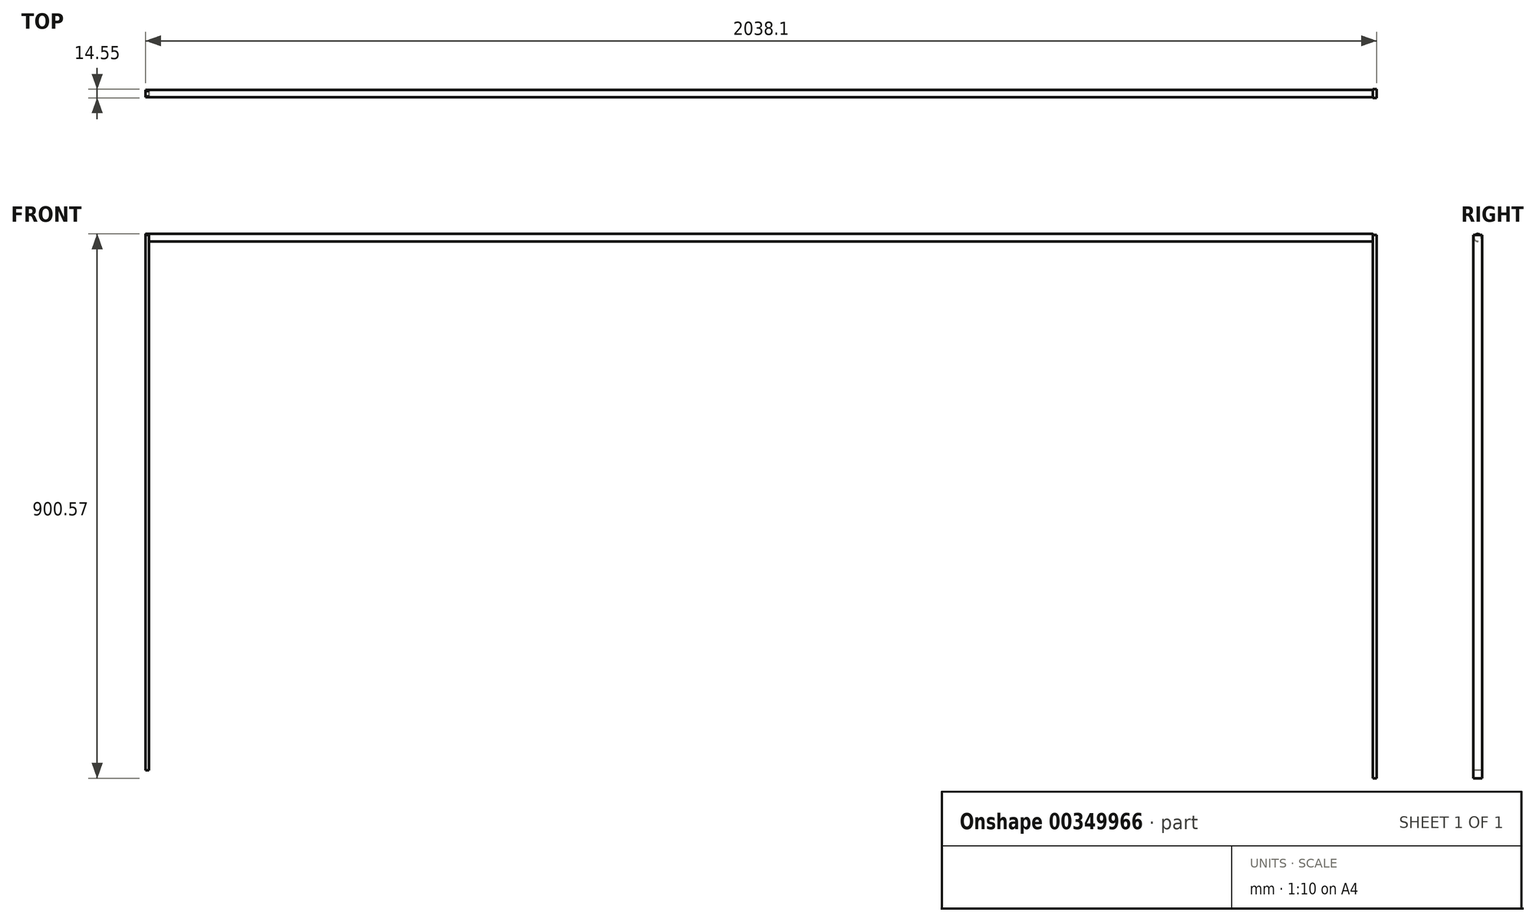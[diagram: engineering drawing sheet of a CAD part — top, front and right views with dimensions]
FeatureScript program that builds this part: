
annotation { "Feature Type Name" : "Feature", "Feature Type Description" : "" }
export const myFeature = defineFeature(function(context is Context, id is Id, definition is map)
    precondition{}
    {
        {
            var Q0;
            Q0=qCreatedBy(makeId("Right.planeOp"),FACE);
            var sketch = newSketch(context, id + "F0", { "sketchPlane" : qUnion([Q0])});
            skCircle(sketch, "E0", {"center": v(-52.21, 53.51) * mm, "radius": 6.09 * mm});
            skSolve(sketch);
        }
        {
            var Q0;
            Q0 = qSketchRegion(id + "F0", true);
            extrude(context, id + "F1", {"entities" : qUnion([Q0]), "depth" : 2032 * mm, "offsetDistance" : 25.4 * mm});
        }
        {
            var Q0;
            Q0=qCreatedBy(makeId("Right.planeOp"),FACE);
            var sketch = newSketch(context, id + "F2", { "sketchPlane" : qUnion([Q0])});
            skLineSegment(sketch, "E1.bottom", {"start": v(-45.98, 57.67) * mm, "end": v(-58.45, 57.67) * mm});
            skLineSegment(sketch, "E1.top", {"start": v(-45.98, -65.98) * mm, "end": v(-58.45, -65.98) * mm});
            skLineSegment(sketch, "E1.left", {"start": v(-45.98, 57.67) * mm, "end": v(-45.98, -65.98) * mm});
            skLineSegment(sketch, "E1.right", {"start": v(-58.45, 57.67) * mm, "end": v(-58.45, -65.98) * mm});
            skSolve(sketch);
        }
        {
            var Q0;
            Q0 = qSketchRegion(id + "F2", true);
            extrude(context, id + "F3", {"entities" : qUnion([Q0]), "operationType" : NewBodyOperationType.ADD, "depth" : 5.33 * mm});
        }
        {
            var Q0;
            Q0=makeQuery(id+"F1.opExtrude","CAP_FACE",FACE,{"disambiguationData":[OSD([sQuery(id+"F0.wireOp",EDGE,"E0")])],"isStart":false});
            var sketch = newSketch(context, id + "F4", { "sketchPlane" : qUnion([Q0])});
            skLineSegment(sketch, "E2.bottom", {"start": v(-59.49, 57.93) * mm, "end": v(-44.94, 57.93) * mm});
            skLineSegment(sketch, "E2.top", {"start": v(-59.49, -78.97) * mm, "end": v(-44.94, -78.97) * mm});
            skLineSegment(sketch, "E2.left", {"start": v(-59.49, 57.93) * mm, "end": v(-59.49, -78.97) * mm});
            skLineSegment(sketch, "E2.right", {"start": v(-44.94, 57.93) * mm, "end": v(-44.94, -78.97) * mm});
            skSolve(sketch);
        }
        {
            var Q0;
            Q0 = qSketchRegion(id + "F4", true);
            extrude(context, id + "F5", {"entities" : qUnion([Q0]), "operationType" : NewBodyOperationType.ADD, "depth" : 6.1 * mm, "offsetDistance" : 25.4 * mm});
        }
        {
            var Q0;
            Q0=makeQuery(id+"F5.opExtrude","SWEPT_FACE",FACE,{"disambiguationData":[OSD([sQuery(id+"F4.wireOp",EDGE,"E2.top")])]});
            var sketch = newSketch(context, id + "F6", { "sketchPlane" : qUnion([Q0])});
            skLineSegment(sketch, "E3.bottom", {"start": v(2038.1, 44.94) * mm, "end": v(2032, 44.94) * mm});
            skLineSegment(sketch, "E3.top", {"start": v(2038.1, 59.49) * mm, "end": v(2032, 59.49) * mm});
            skLineSegment(sketch, "E3.left", {"start": v(2038.1, 44.94) * mm, "end": v(2038.1, 59.49) * mm});
            skLineSegment(sketch, "E3.right", {"start": v(2032, 44.94) * mm, "end": v(2032, 59.49) * mm});
            skSolve(sketch);
        }
        {
            var Q0;
            Q0 = qSketchRegion(id + "F6", true);
            extrude(context, id + "F7", {"entities" : qUnion([Q0]), "operationType" : NewBodyOperationType.ADD, "depth" : 762 * mm, "offsetDistance" : 25.4 * mm});
        }
        {
            var Q0;
            Q0=makeQuery(id+"F3.opExtrude","SWEPT_FACE",FACE,{"disambiguationData":[OSD([sQuery(id+"F2.wireOp",EDGE,"E1.top")])]});
            var sketch = newSketch(context, id + "F8", { "sketchPlane" : qUnion([Q0])});
            skLineSegment(sketch, "E4.bottom", {"start": v(0, 45.98) * mm, "end": v(5.33, 45.98) * mm});
            skLineSegment(sketch, "E4.top", {"start": v(0, 58.45) * mm, "end": v(5.33, 58.45) * mm});
            skLineSegment(sketch, "E4.left", {"start": v(0, 45.98) * mm, "end": v(0, 58.45) * mm});
            skLineSegment(sketch, "E4.right", {"start": v(5.33, 45.98) * mm, "end": v(5.33, 58.45) * mm});
            skSolve(sketch);
        }
        {
            var Q0;
            Q0 = qSketchRegion(id + "F8", true);
            extrude(context, id + "F9", {"entities" : qUnion([Q0]), "operationType" : NewBodyOperationType.ADD, "depth" : 762 * mm, "offsetDistance" : 25.4 * mm});
        }
    });
